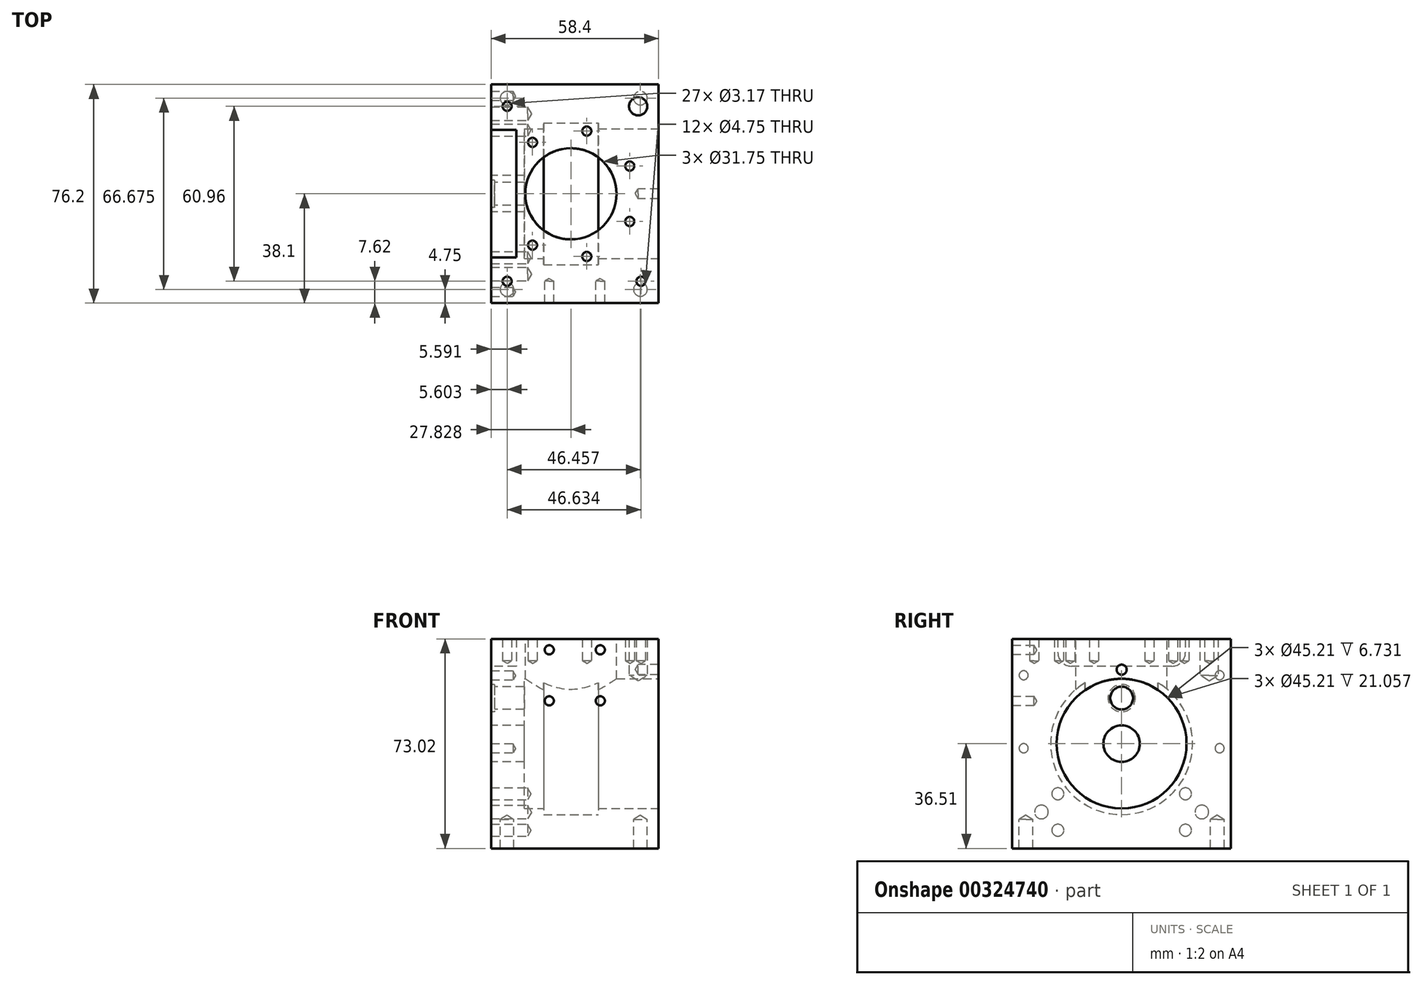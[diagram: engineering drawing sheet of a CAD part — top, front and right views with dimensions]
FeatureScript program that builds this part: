
annotation { "Feature Type Name" : "Feature", "Feature Type Description" : "" }
export const myFeature = defineFeature(function(context is Context, id is Id, definition is map)
    precondition{}
    {
        {
            var Q0;
            Q0=qCreatedBy(makeId("Right.planeOp"),FACE);
            cPlane(context, id + "F0", {"entities" : qUnion([Q0]), "cplaneType" : CPlaneType.OFFSET, "offset" : 1.17 * mm, "oppositeDirection" : true, "width" : 152.4 * mm, "height" : 152.4 * mm});
        }
        {
            var Q0;
            Q0=qCreatedBy(makeId("Front.planeOp"),FACE);
            var sketch = newSketch(context, id + "F1", { "sketchPlane" : qUnion([Q0])});
            skLineSegment(sketch, "E0.bottom", {"start": v(29.2, -36.51) * mm, "end": v(-29.2, -36.51) * mm});
            skLineSegment(sketch, "E0.top", {"start": v(29.2, 36.51) * mm, "end": v(-29.2, 36.51) * mm});
            skLineSegment(sketch, "E0.left", {"start": v(29.2, -36.51) * mm, "end": v(29.2, 36.51) * mm});
            skLineSegment(sketch, "E0.right", {"start": v(-29.2, -36.51) * mm, "end": v(-29.2, 36.51) * mm});
            skPoint(sketch, "E0.middle", {"position": v(0, 0) * mm});
            skSolve(sketch);
        }
        {
            var Q0;
            Q0=makeQuery(id+"F1.imprint","IMPRINT",FACE,{"disambiguationData":[TD([[makeQuery(id+"F1.imprint","IMPRINT",EDGE,{"derivedFrom":sQuery(id+"F1.wireOp",EDGE,"E0.bottom")}),-1.0]])]});
            extrude(context, id + "F2", {"entities" : qUnion([Q0]), "depth" : 76.2 * mm, "symmetric" : true});
        }
        {
            var Q0;
            Q0=makeQuery(id+"F2.opExtrude","SWEPT_FACE",FACE,{"disambiguationData":[OSD([sQuery(id+"F1.wireOp",EDGE,"E0.left")])]});
            var sketch = newSketch(context, id + "F3", { "sketchPlane" : qUnion([Q0])});
            skCircle(sketch, "E1", {"center": v(0, 0) * mm, "radius": 22.6 * mm});
            skSolve(sketch);
        }
        {
            var Q0;
            Q0=makeQuery(id+"F3.imprint","IMPRINT",FACE,{"disambiguationData":[TD([[makeQuery(id+"F3.imprint","IMPRINT",EDGE,{"derivedFrom":sQuery(id+"F3.wireOp",EDGE,"E1")}),1.0]])]});
            extrude(context, id + "F4", {"entities" : qUnion([Q0]), "operationType" : NewBodyOperationType.REMOVE, "oppositeDirection" : true, "depth" : 46.84 * mm});
        }
        {
            var Q0;
            Q0=makeQuery(id+"F2.opExtrude","SWEPT_FACE",FACE,{"disambiguationData":[OSD([sQuery(id+"F1.wireOp",EDGE,"E0.top")])]});
            var sketch = newSketch(context, id + "F5", { "sketchPlane" : qUnion([Q0])});
            skCircle(sketch, "E2", {"center": v(-1.37, 0) * mm, "radius": 15.88 * mm});
            skSolve(sketch);
        }
        {
            var Q0;
            Q0=makeQuery(id+"F5.imprint","IMPRINT",FACE,{"disambiguationData":[TD([[makeQuery(id+"F5.imprint","IMPRINT",EDGE,{"derivedFrom":sQuery(id+"F5.wireOp",EDGE,"qw90dT9u-hNCC-apiM-7iwq-9HIEZ2rtUqi5")}),1.0]])]});
            var Q1;
            Q1=makeQuery(id+"F5.imprint","IMPRINT",FACE,{"disambiguationData":[TD([[makeQuery(id+"F5.imprint","IMPRINT",EDGE,{"derivedFrom":sQuery(id+"F5.wireOp",EDGE,"E2")}),1.0]])]});
            extrude(context, id + "F6", {"entities" : qUnion([Q0, Q1]), "operationType" : NewBodyOperationType.REMOVE, "oppositeDirection" : true, "depth" : 38.1 * mm, "offsetDistance" : 25.4 * mm});
        }
        {
            var Q0;
            Q0=makeQuery(id+"F2.opExtrude","SWEPT_FACE",FACE,{"disambiguationData":[OSD([sQuery(id+"F1.wireOp",EDGE,"E0.left")])]});
            cPlane(context, id + "F7", {"entities" : qUnion([Q0]), "cplaneType" : CPlaneType.OFFSET, "offset" : 21.06 * mm, "oppositeDirection" : true, "width" : 152.4 * mm, "height" : 152.4 * mm});
        }
        {
            var Q0;
            Q0=qCreatedBy(id+"F7.planeOp",FACE);
            var sketch = newSketch(context, id + "F8", { "sketchPlane" : qUnion([Q0])});
            skCircle(sketch, "E3", {"center": v(0, 0) * mm, "radius": 24.74 * mm});
            skSolve(sketch);
        }
        {
            var Q0;
            Q0=makeQuery(id+"F8.imprint","IMPRINT",FACE,{"disambiguationData":[TD([[makeQuery(id+"F8.imprint","IMPRINT",EDGE,{"derivedFrom":sQuery(id+"F8.wireOp",EDGE,"E3")}),1.0]])]});
            extrude(context, id + "F9", {"entities" : qUnion([Q0]), "operationType" : NewBodyOperationType.REMOVE, "oppositeDirection" : true, "depth" : 19.05 * mm});
        }
        {
            var Q0;
            Q0=makeQuery(id+"F2.opExtrude","SWEPT_FACE",FACE,{"disambiguationData":[OSD([sQuery(id+"F1.wireOp",EDGE,"E0.right")])]});
            var sketch = newSketch(context, id + "F10", { "sketchPlane" : qUnion([Q0])});
            skCircle(sketch, "E4", {"center": v(0, 0) * mm, "radius": 6.35 * mm});
            skSolve(sketch);
        }
        {
            var Q0;
            Q0=makeQuery(id+"F10.imprint","IMPRINT",FACE,{"disambiguationData":[TD([[makeQuery(id+"F10.imprint","IMPRINT",EDGE,{"derivedFrom":sQuery(id+"F10.wireOp",EDGE,"E4")}),1.0]])]});
            extrude(context, id + "F11", {"entities" : qUnion([Q0]), "operationType" : NewBodyOperationType.REMOVE, "oppositeDirection" : true, "depth" : 25.4 * mm});
        }
        {
            var Q0;
            Q0=makeQuery(id+"F2.opExtrude","SWEPT_FACE",FACE,{"disambiguationData":[OSD([sQuery(id+"F1.wireOp",EDGE,"E0.right")])]});
            var sketch = newSketch(context, id + "F12", { "sketchPlane" : qUnion([Q0])});
            skLineSegment(sketch, "E5.bottom", {"start": v(-22.22, 36.51) * mm, "end": v(22.22, 36.51) * mm});
            skLineSegment(sketch, "E5.top", {"start": v(-17.46, 26.99) * mm, "end": v(17.46, 26.99) * mm});
            skLineSegment(sketch, "E5.left", {"start": v(-22.23, 36.51) * mm, "end": v(-22.23, 31.75) * mm});
            skLineSegment(sketch, "E5.right", {"start": v(22.23, 36.51) * mm, "end": v(22.23, 31.75) * mm});
            skPoint(sketch, "E6.visualSharp", {"position": v(-22.23, 26.99) * mm});
            skArc(sketch, "E6.filletArc", {"start": v(-22.23, 31.75) * mm, "mid": v(-20.83, 28.38) * mm, "end": v(-17.46, 26.99) * mm});
            skPoint(sketch, "E7.visualSharp", {"position": v(22.23, 26.99) * mm});
            skArc(sketch, "E7.filletArc", {"start": v(17.46, 26.99) * mm, "mid": v(20.83, 28.38) * mm, "end": v(22.22, 31.75) * mm});
            skSolve(sketch);
        }
        {
            var Q0;
            Q0=makeQuery(id+"F12.imprint","IMPRINT",FACE,{"disambiguationData":[TD([[makeQuery(id+"F12.imprint","IMPRINT",EDGE,{"derivedFrom":sQuery(id+"F12.wireOp",EDGE,"E5.bottom")}),1.0]])]});
            extrude(context, id + "F13", {"entities" : qUnion([Q0]), "operationType" : NewBodyOperationType.REMOVE, "oppositeDirection" : true, "depth" : 8.76 * mm});
        }
        {
            var Q0;
            Q0=makeQuery(id+"F2.opExtrude","SWEPT_FACE",FACE,{"disambiguationData":[OSD([sQuery(id+"F1.wireOp",EDGE,"E0.right")])]});
            var sketch = newSketch(context, id + "F14", { "sketchPlane" : qUnion([Q0])});
            skCircle(sketch, "E8", {"center": v(0, 15.88) * mm, "radius": 3.97 * mm});
            skSolve(sketch);
        }
        {
            var Q0;
            Q0=makeQuery(id+"F14.imprint","IMPRINT",FACE,{"disambiguationData":[TD([[makeQuery(id+"F14.imprint","IMPRINT",EDGE,{"derivedFrom":sQuery(id+"F14.wireOp",EDGE,"E8")}),1.0]])]});
            extrude(context, id + "F15", {"entities" : qUnion([Q0]), "operationType" : NewBodyOperationType.REMOVE, "oppositeDirection" : true, "depth" : 25.4 * mm});
        }
        {
            var Q0;
            Q0=makeQuery(id+"F2.opExtrude","SWEPT_FACE",FACE,{"disambiguationData":[OSD([sQuery(id+"F1.wireOp",EDGE,"E0.right")])]});
            var sketch = newSketch(context, id + "F16", { "sketchPlane" : qUnion([Q0])});
            skCircle(sketch, "E9", {"center": v(0, 15.87) * mm, "radius": 4.76 * mm});
            skSolve(sketch);
        }
        {
            var Q0;
            Q0=makeQuery(id+"F16.imprint","IMPRINT",FACE,{"disambiguationData":[TD([[makeQuery(id+"F16.imprint","IMPRINT",EDGE,{"derivedFrom":sQuery(id+"F16.wireOp",EDGE,"E9")}),1.0]])]});
            extrude(context, id + "F17", {"entities" : qUnion([Q0]), "operationType" : NewBodyOperationType.REMOVE, "oppositeDirection" : true, "depth" : 1.14 * mm});
        }
        {
            var Q0;
            Q0=makeQuery(id+"F2.opExtrude","SWEPT_FACE",FACE,{"disambiguationData":[OSD([sQuery(id+"F1.wireOp",EDGE,"E0.right")])]});
            var sketch = newSketch(context, id + "F18", { "sketchPlane" : qUnion([Q0])});
            skPoint(sketch, "E10", {"position": v(-27.94, -23.83) * mm});
            skPoint(sketch, "E11", {"position": v(27.94, -23.83) * mm});
            skSolve(sketch);
        }
        {
            var Q0;
            Q0=sQuery(id+"F18.wireOp",VERTEX,"E10");
            var Q1;
            Q1=sQuery(id+"F18.wireOp",VERTEX,"E11");
            var Q2;
            Q2=makeQuery(id+"F2.opExtrude","SWEPT_BODY",BODY,{"disambiguationData":[OSD([sQuery(id+"F1.wireOp",EDGE,"E0.bottom"),sQuery(id+"F1.wireOp",EDGE,"E0.top"),sQuery(id+"F1.wireOp",EDGE,"E0.left"),sQuery(id+"F1.wireOp",EDGE,"E0.right")])]});
            hole(context, id + "F19", {"style" : HoleStyle.SIMPLE, "endStyle" : HoleEndStyle.BLIND, "holeDiameter" : 4.76 * mm, "holeDepth" : 12.7 * mm, "tappedDepth" : 12.7 * mm, "tapClearance" : 3, "locations" : qUnion([Q0, Q1]), "scope" : qUnion([Q2])});
        }
        {
            var Q0;
            Q0=makeQuery(id+"F2.opExtrude","SWEPT_FACE",FACE,{"disambiguationData":[OSD([sQuery(id+"F1.wireOp",EDGE,"E0.left")])]});
            var sketch = newSketch(context, id + "F20", { "sketchPlane" : qUnion([Q0])});
            skPoint(sketch, "E12", {"position": v(0, 25.78) * mm});
            skSolve(sketch);
        }
        {
            var Q0;
            Q0=sQuery(id+"F20.wireOp",VERTEX,"E12");
            var Q1;
            Q1=makeQuery(id+"F2.opExtrude","SWEPT_BODY",BODY,{"disambiguationData":[OSD([sQuery(id+"F1.wireOp",EDGE,"E0.bottom"),sQuery(id+"F1.wireOp",EDGE,"E0.top"),sQuery(id+"F1.wireOp",EDGE,"E0.left"),sQuery(id+"F1.wireOp",EDGE,"E0.right")])]});
            hole(context, id + "F21", {"style" : HoleStyle.SIMPLE, "endStyle" : HoleEndStyle.BLIND, "holeDiameter" : 3.5 * mm, "holeDepth" : 7.11 * mm, "tappedDepth" : 12.7 * mm, "tapClearance" : 3, "locations" : qUnion([Q0]), "scope" : qUnion([Q1]), "majorDiameter" : 6.35 * mm});
        }
        {
            var Q0;
            Q0=makeQuery(id+"F2.opExtrude","SWEPT_FACE",FACE,{"disambiguationData":[OSD([sQuery(id+"F1.wireOp",EDGE,"E0.top")])]});
            var sketch = newSketch(context, id + "F22", { "sketchPlane" : qUnion([Q0])});
            skPoint(sketch, "E13", {"position": v(-23.6, 30.48) * mm});
            skPoint(sketch, "E14", {"position": v(23.04, -30.48) * mm});
            skPoint(sketch, "E15", {"position": v(-23.6, -30.48) * mm});
            skSolve(sketch);
        }
        {
            var Q0;
            Q0=sQuery(id+"F22.wireOp",VERTEX,"E13");
            var Q1;
            Q1=sQuery(id+"F22.wireOp",VERTEX,"14cf712f-8334-4a4b-b4a6-a5b53970bc37");
            var Q2;
            Q2=sQuery(id+"F22.wireOp",VERTEX,"E14");
            var Q3;
            Q3=sQuery(id+"F22.wireOp",VERTEX,"E15");
            var Q4;
            Q4=makeQuery(id+"F2.opExtrude","SWEPT_BODY",BODY,{"disambiguationData":[OSD([sQuery(id+"F1.wireOp",EDGE,"E0.bottom"),sQuery(id+"F1.wireOp",EDGE,"E0.top"),sQuery(id+"F1.wireOp",EDGE,"E0.left"),sQuery(id+"F1.wireOp",EDGE,"E0.right")])]});
            hole(context, id + "F23", {"style" : HoleStyle.SIMPLE, "endStyle" : HoleEndStyle.BLIND, "holeDiameter" : 3.17 * mm, "holeDepth" : 7.62 * mm, "tappedDepth" : 12.7 * mm, "tapClearance" : 3, "locations" : qUnion([Q0, Q1, Q2, Q3]), "scope" : qUnion([Q4]), "majorDiameter" : 6.35 * mm});
        }
        {
            var Q0;
            Q0=makeQuery(id+"F2.opExtrude","SWEPT_FACE",FACE,{"disambiguationData":[OSD([sQuery(id+"F1.wireOp",EDGE,"E0.top")])]});
            var sketch = newSketch(context, id + "F24", { "sketchPlane" : qUnion([Q0])});
            skPoint(sketch, "E16", {"position": v(4.17, 21.84) * mm});
            skPoint(sketch, "E17", {"position": v(4.17, -21.84) * mm});
            skPoint(sketch, "E18", {"position": v(19.13, 9.65) * mm});
            skPoint(sketch, "E19", {"position": v(19.13, -9.65) * mm});
            skPoint(sketch, "E20", {"position": v(-14.73, 17.9) * mm});
            skPoint(sketch, "E21", {"position": v(-14.73, -17.9) * mm});
            skSolve(sketch);
        }
        {
            var Q0;
            Q0=sQuery(id+"F24.wireOp",VERTEX,"E20");
            var Q1;
            Q1=sQuery(id+"F24.wireOp",VERTEX,"E16");
            var Q2;
            Q2=sQuery(id+"F24.wireOp",VERTEX,"E18");
            var Q3;
            Q3=sQuery(id+"F24.wireOp",VERTEX,"E19");
            var Q4;
            Q4=sQuery(id+"F24.wireOp",VERTEX,"E17");
            var Q5;
            Q5=sQuery(id+"F24.wireOp",VERTEX,"E21");
            var Q6;
            Q6=makeQuery(id+"F2.opExtrude","SWEPT_BODY",BODY,{"disambiguationData":[OSD([sQuery(id+"F1.wireOp",EDGE,"E0.bottom"),sQuery(id+"F1.wireOp",EDGE,"E0.top"),sQuery(id+"F1.wireOp",EDGE,"E0.left"),sQuery(id+"F1.wireOp",EDGE,"E0.right")])]});
            hole(context, id + "F25", {"style" : HoleStyle.SIMPLE, "endStyle" : HoleEndStyle.BLIND, "holeDiameter" : 3.17 * mm, "holeDepth" : 7.62 * mm, "tappedDepth" : 12.7 * mm, "tapClearance" : 3, "locations" : qUnion([Q0, Q1, Q2, Q3, Q4, Q5]), "scope" : qUnion([Q6])});
        }
        {
            var Q0;
            Q0=makeQuery(id+"F2.opExtrude","SWEPT_FACE",FACE,{"disambiguationData":[OSD([sQuery(id+"F1.wireOp",EDGE,"E0.right")])]});
            var sketch = newSketch(context, id + "F26", { "sketchPlane" : qUnion([Q0])});
            skPoint(sketch, "E22", {"position": v(34.14, 23.83) * mm});
            skPoint(sketch, "E23", {"position": v(34.14, -1.6) * mm});
            skPoint(sketch, "E24", {"position": v(-34.14, -1.6) * mm});
            skPoint(sketch, "E25", {"position": v(-34.14, 23.83) * mm});
            skSolve(sketch);
        }
        {
            var Q0;
            Q0=sQuery(id+"F26.wireOp",VERTEX,"E25");
            var Q1;
            Q1=sQuery(id+"F26.wireOp",VERTEX,"E22");
            var Q2;
            Q2=sQuery(id+"F26.wireOp",VERTEX,"E23");
            var Q3;
            Q3=sQuery(id+"F26.wireOp",VERTEX,"E24");
            var Q4;
            Q4=makeQuery(id+"F2.opExtrude","SWEPT_BODY",BODY,{"disambiguationData":[OSD([sQuery(id+"F1.wireOp",EDGE,"E0.bottom"),sQuery(id+"F1.wireOp",EDGE,"E0.top"),sQuery(id+"F1.wireOp",EDGE,"E0.left"),sQuery(id+"F1.wireOp",EDGE,"E0.right")])]});
            hole(context, id + "F27", {"style" : HoleStyle.SIMPLE, "endStyle" : HoleEndStyle.BLIND, "holeDiameter" : 3.17 * mm, "holeDepth" : 7.62 * mm, "tappedDepth" : 12.7 * mm, "tapClearance" : 3, "locations" : qUnion([Q0, Q1, Q2, Q3]), "scope" : qUnion([Q4])});
        }
        {
            var Q0;
            Q0=makeQuery(id+"F2.opExtrude","SWEPT_FACE",FACE,{"disambiguationData":[OSD([sQuery(id+"F1.wireOp",EDGE,"E0.right")])]});
            var sketch = newSketch(context, id + "F28", { "sketchPlane" : qUnion([Q0])});
            skPoint(sketch, "E26", {"position": v(22.23, -17.48) * mm});
            skPoint(sketch, "E27", {"position": v(22.23, -30.18) * mm});
            skPoint(sketch, "E28", {"position": v(-22.23, -30.18) * mm});
            skPoint(sketch, "E29", {"position": v(-22.23, -17.48) * mm});
            skSolve(sketch);
        }
        {
            var Q0;
            Q0=sQuery(id+"F28.wireOp",VERTEX,"E29");
            var Q1;
            Q1=sQuery(id+"F28.wireOp",VERTEX,"E28");
            var Q2;
            Q2=sQuery(id+"F28.wireOp",VERTEX,"E26");
            var Q3;
            Q3=sQuery(id+"F28.wireOp",VERTEX,"E27");
            var Q4;
            Q4=makeQuery(id+"F2.opExtrude","SWEPT_BODY",BODY,{"disambiguationData":[OSD([sQuery(id+"F1.wireOp",EDGE,"E0.bottom"),sQuery(id+"F1.wireOp",EDGE,"E0.top"),sQuery(id+"F1.wireOp",EDGE,"E0.left"),sQuery(id+"F1.wireOp",EDGE,"E0.right")])]});
            hole(context, id + "F29", {"style" : HoleStyle.SIMPLE, "endStyle" : HoleEndStyle.BLIND, "holeDiameter" : 4.17 * mm, "holeDepth" : 12.7 * mm, "tappedDepth" : 12.7 * mm, "tapClearance" : 3, "locations" : qUnion([Q0, Q1, Q2, Q3]), "scope" : qUnion([Q4])});
        }
        {
            var Q0;
            Q0=makeQuery(id+"F2.opExtrude","SWEPT_FACE",FACE,{"disambiguationData":[OSD([sQuery(id+"F1.wireOp",EDGE,"E0.bottom")])]});
            var sketch = newSketch(context, id + "F30", { "sketchPlane" : qUnion([Q0])});
            skPoint(sketch, "E30", {"position": v(-23.6, -33.32) * mm});
            skPoint(sketch, "E31", {"position": v(22.85, -33.32) * mm});
            skPoint(sketch, "E32", {"position": v(22.85, 33.35) * mm});
            skPoint(sketch, "E33", {"position": v(-23.6, 33.35) * mm});
            skSolve(sketch);
        }
        {
            var Q0;
            Q0=sQuery(id+"F30.wireOp",VERTEX,"E33");
            var Q1;
            Q1=sQuery(id+"F30.wireOp",VERTEX,"E32");
            var Q2;
            Q2=sQuery(id+"F30.wireOp",VERTEX,"E31");
            var Q3;
            Q3=sQuery(id+"F30.wireOp",VERTEX,"E30");
            var Q4;
            Q4=makeQuery(id+"F2.opExtrude","SWEPT_BODY",BODY,{"disambiguationData":[OSD([sQuery(id+"F1.wireOp",EDGE,"E0.bottom"),sQuery(id+"F1.wireOp",EDGE,"E0.top"),sQuery(id+"F1.wireOp",EDGE,"E0.left"),sQuery(id+"F1.wireOp",EDGE,"E0.right")])]});
            hole(context, id + "F31", {"style" : HoleStyle.SIMPLE, "endStyle" : HoleEndStyle.BLIND, "holeDiameter" : 4.75 * mm, "holeDepth" : 10.16 * mm, "tappedDepth" : 12.7 * mm, "tapClearance" : 3, "locations" : qUnion([Q0, Q1, Q2, Q3]), "scope" : qUnion([Q4])});
        }
        {
            var Q0;
            Q0=makeQuery(id+"F2.opExtrude","CAP_FACE",FACE,{"disambiguationData":[OSD([sQuery(id+"F1.wireOp",EDGE,"E0.bottom"),sQuery(id+"F1.wireOp",EDGE,"E0.top"),sQuery(id+"F1.wireOp",EDGE,"E0.left"),sQuery(id+"F1.wireOp",EDGE,"E0.right")])],"isStart":false});
            var sketch = newSketch(context, id + "F32", { "sketchPlane" : qUnion([Q0])});
            skPoint(sketch, "E34", {"position": v(-8.9, 32.7) * mm});
            skPoint(sketch, "E35", {"position": v(8.88, 32.7) * mm});
            skPoint(sketch, "E36", {"position": v(8.88, 14.92) * mm});
            skPoint(sketch, "E37", {"position": v(-8.9, 14.92) * mm});
            skSolve(sketch);
        }
        {
            var Q0;
            Q0=sQuery(id+"F32.wireOp",VERTEX,"E34");
            var Q1;
            Q1=sQuery(id+"F32.wireOp",VERTEX,"E35");
            var Q2;
            Q2=sQuery(id+"F32.wireOp",VERTEX,"E36");
            var Q3;
            Q3=sQuery(id+"F32.wireOp",VERTEX,"E37");
            var Q4;
            Q4=makeQuery(id+"F2.opExtrude","SWEPT_BODY",BODY,{"disambiguationData":[OSD([sQuery(id+"F1.wireOp",EDGE,"E0.bottom"),sQuery(id+"F1.wireOp",EDGE,"E0.top"),sQuery(id+"F1.wireOp",EDGE,"E0.left"),sQuery(id+"F1.wireOp",EDGE,"E0.right")])]});
            hole(context, id + "F33", {"style" : HoleStyle.SIMPLE, "endStyle" : HoleEndStyle.BLIND, "holeDiameter" : 3.17 * mm, "holeDepth" : 7.62 * mm, "tappedDepth" : 12.7 * mm, "tapClearance" : 3, "locations" : qUnion([Q0, Q1, Q2, Q3]), "scope" : qUnion([Q4])});
        }
        {
            var Q0;
            Q0=makeQuery(id+"F2.opExtrude","SWEPT_FACE",FACE,{"disambiguationData":[OSD([sQuery(id+"F1.wireOp",EDGE,"E0.top")])]});
            var sketch = newSketch(context, id + "F34", { "sketchPlane" : qUnion([Q0])});
            skPoint(sketch, "E38", {"position": v(22.09, 30.48) * mm});
            skSolve(sketch);
        }
        {
            var Q0;
            Q0=sQuery(id+"F34.wireOp",VERTEX,"E38");
            var Q1;
            Q1=makeQuery(id+"F2.opExtrude","SWEPT_BODY",BODY,{"disambiguationData":[OSD([sQuery(id+"F1.wireOp",EDGE,"E0.bottom"),sQuery(id+"F1.wireOp",EDGE,"E0.top"),sQuery(id+"F1.wireOp",EDGE,"E0.left"),sQuery(id+"F1.wireOp",EDGE,"E0.right")])]});
            hole(context, id + "F35", {"style" : HoleStyle.SIMPLE, "endStyle" : HoleEndStyle.BLIND, "holeDiameter" : 6.35 * mm, "majorDiameter" : 6.35 * mm, "holeDepth" : 12.7 * mm, "tappedDepth" : 12.7 * mm, "tapClearance" : 3, "locations" : qUnion([Q0]), "scope" : qUnion([Q1])});
        }
    });
